# Revit family: Precast Stemmed Deck Members-Single Tee-Side
name_source: partatom
category: Detail Items
revit_build: Autodesk Revit Architecture 2012 (Build: 20110210_1515)
units: mm (PartAtom-declared; Revit-internal decimal feet)

## types (8) — shared parameters
Bottom Tee Width = 0' - 8"
Slab Depth = 0' - 1 1/2"
Space = 0' - 0"
Top Tee Width = 0' - 8"

## per-type parameters (varying)
| type | Depth | Keynote | Tdepth | Width |
| 8ST36 | 3' - 0" | 03 41 00.G37 | 0' - 0" | 8' - 0" |
| 8ST36+2 | 3' - 0" | 03 41 00.G38 | 0' - 2" | 8' - 0" |
| 8LST36 | 3' - 0" | 03 41 00.G39 | 0' - 0" | 8' - 0" |
| 8LST36+2 | 3' - 0" | 03 41 00.G40 | 0' - 2" | 8' - 0" |
| 10ST36 | 3' - 0" | 03 41 00.G41 | 0' - 0" | 10' - 0" |
| 10LST36 | 3' - 0" | 03 41 00.G42 | 0' - 0" | 10' - 0" |
| 10ST48 | 4' - 0" | 03 41 00.G43 | 0' - 0" | 10' - 0" |
| 10LST48 | 4' - 0" | 03 41 00.G44 | 0' - 0" | 10' - 0" |

## geometry (parser evidence)
native form markers: Sweep x1
no freeform markers — native parametric forms only
